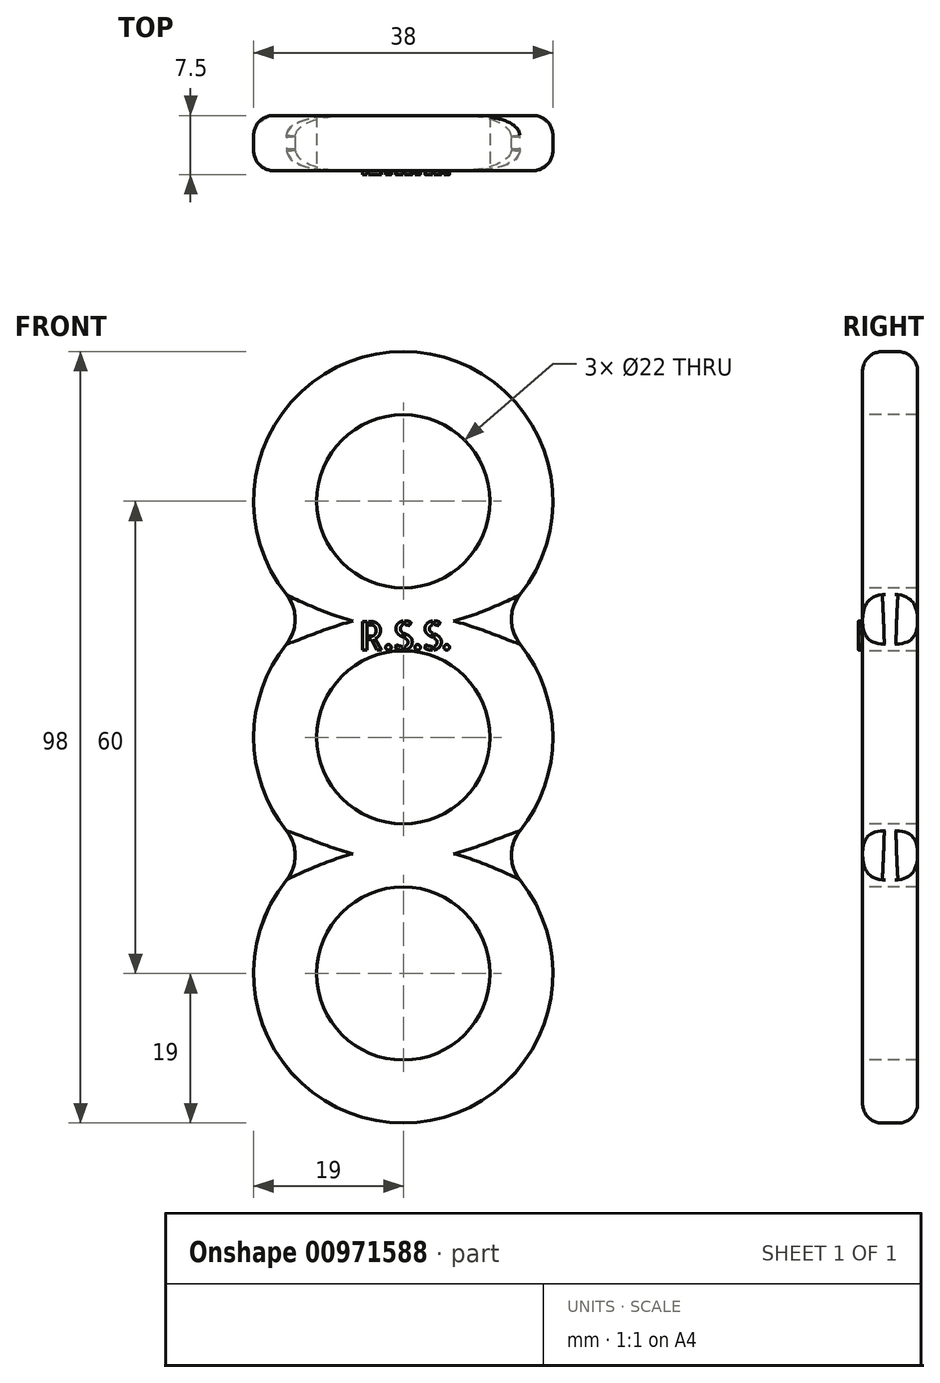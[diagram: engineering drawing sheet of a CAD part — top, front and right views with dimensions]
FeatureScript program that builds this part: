
annotation { "Feature Type Name" : "Feature", "Feature Type Description" : "" }
export const myFeature = defineFeature(function(context is Context, id is Id, definition is map)
    precondition{}
    {
        {
            var Q0;
            Q0=qCreatedBy(makeId("Front.planeOp"),FACE);
            var sketch = newSketch(context, id + "F0", { "sketchPlane" : qUnion([Q0])});
            skCircle(sketch, "E0", {"center": v(0, 0) * mm, "radius": 19 * mm});
            skSolve(sketch);
        }
        {
            var Q0;
            Q0=makeQuery(id+"F0.imprint","IMPRINT",FACE,{"disambiguationData":[TD([[makeQuery(id+"F0.imprint","IMPRINT",EDGE,{"derivedFrom":sQuery(id+"F0.wireOp",EDGE,"E0")}),1.0]])]});
            extrude(context, id + "F1", {"entities" : qUnion([Q0]), "depth" : 7 * mm, "offsetDistance" : 25 * mm});
        }
        {
            var Q0;
            Q0=makeQuery(id+"F1.opExtrude","CAP_FACE",FACE,{"disambiguationData":[OSD([sQuery(id+"F0.wireOp",EDGE,"E0")])],"isStart":false});
            var sketch = newSketch(context, id + "F2", { "sketchPlane" : qUnion([Q0])});
            skCircle(sketch, "E1", {"center": v(0, 0) * mm, "radius": 11 * mm});
            skSolve(sketch);
        }
        {
            var Q0;
            Q0=sQuery(id+"F2.wireOp",VERTEX,"E1.center");
            var Q1;
            Q1=makeQuery(id+"F1.opExtrude","SWEPT_BODY",BODY,{"disambiguationData":[OSD([sQuery(id+"F0.wireOp",EDGE,"E0")])]});
            hole(context, id + "F3", {"style" : HoleStyle.SIMPLE, "endStyle" : HoleEndStyle.THROUGH, "holeDiameter" : 22 * mm, "majorDiameter" : 5 * mm, "isTappedThrough" : true, "tappedDepth" : 12 * mm, "tapClearance" : 3, "locations" : qUnion([Q0]), "scope" : qUnion([Q1])});
        }
        {
            var Q0;
            Q0=qCreatedBy(makeId("Front.planeOp"),FACE);
            var sketch = newSketch(context, id + "F4", { "sketchPlane" : qUnion([Q0])});
            skCircle(sketch, "E2", {"center": v(0, 30) * mm, "radius": 19 * mm});
            skSolve(sketch);
        }
        {
            var Q0;
            Q0=qCreatedBy(makeId("Front.planeOp"),FACE);
            var sketch = newSketch(context, id + "F5", { "sketchPlane" : qUnion([Q0])});
            skCircle(sketch, "E3", {"center": v(0, -30) * mm, "radius": 19 * mm});
            skSolve(sketch);
        }
        {
            var Q0;
            Q0=makeQuery(id+"F4.imprint","IMPRINT",FACE,{"disambiguationData":[TD([[makeQuery(id+"F4.imprint","IMPRINT",EDGE,{"derivedFrom":sQuery(id+"F4.wireOp",EDGE,"E2")}),1.0]])]});
            extrude(context, id + "F6", {"entities" : qUnion([Q0]), "operationType" : NewBodyOperationType.ADD, "depth" : 7 * mm, "offsetDistance" : 25 * mm});
        }
        {
            var Q0;
            Q0=makeQuery(id+"F5.imprint","IMPRINT",FACE,{"disambiguationData":[TD([[makeQuery(id+"F5.imprint","IMPRINT",EDGE,{"derivedFrom":sQuery(id+"F5.wireOp",EDGE,"E3")}),1.0]])]});
            extrude(context, id + "F7", {"entities" : qUnion([Q0]), "operationType" : NewBodyOperationType.ADD, "depth" : 7 * mm, "offsetDistance" : 25 * mm});
        }
        {
            var Q0;
            Q0=makeQuery(id+"F7.boolean.opBoolean","MERGE",FACE,{"derivedFrom":[makeQuery(id+"F6.boolean.opBoolean","MERGE",FACE,{"derivedFrom":[makeQuery(id+"F1.opExtrude","CAP_FACE",FACE,{"disambiguationData":[OSD([sQuery(id+"F0.wireOp",EDGE,"E0")])],"isStart":false}),makeQuery(id+"F6.opExtrude","CAP_FACE",FACE,{"disambiguationData":[OSD([sQuery(id+"F4.wireOp",EDGE,"E2")])],"isStart":false})]}),makeQuery(id+"F7.opExtrude","CAP_FACE",FACE,{"disambiguationData":[OSD([sQuery(id+"F5.wireOp",EDGE,"E3")])],"isStart":false})]});
            var sketch = newSketch(context, id + "F8", { "sketchPlane" : qUnion([Q0])});
            skCircle(sketch, "E4", {"center": v(0, 30) * mm, "radius": 11.47 * mm});
            skSolve(sketch);
        }
        {
            var Q0;
            Q0=sQuery(id+"F8.wireOp",VERTEX,"E4.center");
            var Q1;
            Q1=makeQuery(id+"F1.opExtrude","SWEPT_BODY",BODY,{"disambiguationData":[OSD([sQuery(id+"F0.wireOp",EDGE,"E0")])]});
            hole(context, id + "F9", {"style" : HoleStyle.SIMPLE, "endStyle" : HoleEndStyle.THROUGH, "holeDiameter" : 22 * mm, "majorDiameter" : 5 * mm, "isTappedThrough" : true, "tappedDepth" : 12 * mm, "tapClearance" : 3, "locations" : qUnion([Q0]), "scope" : qUnion([Q1])});
        }
        {
            var Q0;
            Q0=makeQuery(id+"F7.boolean.opBoolean","MERGE",FACE,{"derivedFrom":[makeQuery(id+"F6.boolean.opBoolean","MERGE",FACE,{"derivedFrom":[makeQuery(id+"F1.opExtrude","CAP_FACE",FACE,{"disambiguationData":[OSD([sQuery(id+"F0.wireOp",EDGE,"E0")])],"isStart":false}),makeQuery(id+"F6.opExtrude","CAP_FACE",FACE,{"disambiguationData":[OSD([sQuery(id+"F4.wireOp",EDGE,"E2")])],"isStart":false})]}),makeQuery(id+"F7.opExtrude","CAP_FACE",FACE,{"disambiguationData":[OSD([sQuery(id+"F5.wireOp",EDGE,"E3")])],"isStart":false})]});
            var sketch = newSketch(context, id + "F10", { "sketchPlane" : qUnion([Q0])});
            skCircle(sketch, "E5", {"center": v(0, -30) * mm, "radius": 11.34 * mm});
            skSolve(sketch);
        }
        {
            var Q0;
            Q0=sQuery(id+"F10.wireOp",VERTEX,"E5.center");
            var Q1;
            Q1=makeQuery(id+"F1.opExtrude","SWEPT_BODY",BODY,{"disambiguationData":[OSD([sQuery(id+"F0.wireOp",EDGE,"E0")])]});
            hole(context, id + "F11", {"style" : HoleStyle.SIMPLE, "endStyle" : HoleEndStyle.THROUGH, "holeDiameter" : 22 * mm, "majorDiameter" : 5 * mm, "isTappedThrough" : true, "tappedDepth" : 12 * mm, "tapClearance" : 3, "locations" : qUnion([Q0]), "scope" : qUnion([Q1])});
        }
        {
            var Q0;
            Q0=makeQuery(id+"F6.opExtrude","CAP_EDGE",EDGE,{"disambiguationData":[OSD([sQuery(id+"F4.wireOp",EDGE,"E2")])],"isStart":false});
            fillet(context, id + "F12", {"entities" : qUnion([Q0]), "radius" : 2.5 * mm, "tangentPropagation" : true, "allowEdgeOverflow" : false});
        }
        {
            var Q0;
            Q0=makeQuery(id+"F6.opExtrude","CAP_EDGE",EDGE,{"disambiguationData":[OSD([sQuery(id+"F4.wireOp",EDGE,"E2")])],"isStart":true});
            fillet(context, id + "F13", {"entities" : qUnion([Q0]), "radius" : 2.5 * mm, "tangentPropagation" : true, "allowEdgeOverflow" : false});
        }
        {
            var Q0;
            Q0=makeQuery(id+"F7.boolean.opBoolean","SPLIT",EDGE,{"disambiguationData":[OD(1.0)],"derivedFrom":makeQuery(id+"F1.opExtrude","CAP_EDGE",EDGE,{"disambiguationData":[OSD([sQuery(id+"F0.wireOp",EDGE,"E0")])],"isStart":false})});
            fillet(context, id + "F14", {"entities" : qUnion([Q0]), "radius" : 2.9 * mm, "tangentPropagation" : true, "allowEdgeOverflow" : false});
        }
        {
            var Q0;
            Q0=makeQuery(id+"F7.boolean.opBoolean","SPLIT",EDGE,{"disambiguationData":[OD(0.0)],"derivedFrom":makeQuery(id+"F1.opExtrude","CAP_EDGE",EDGE,{"disambiguationData":[OSD([sQuery(id+"F0.wireOp",EDGE,"E0")])],"isStart":false})});
            fillet(context, id + "F15", {"entities" : qUnion([Q0]), "radius" : 2.9 * mm, "tangentPropagation" : true, "allowEdgeOverflow" : false});
        }
        {
            var Q0;
            Q0=makeQuery(id+"F7.opExtrude","CAP_EDGE",EDGE,{"disambiguationData":[OSD([sQuery(id+"F5.wireOp",EDGE,"E3")])],"isStart":false});
            fillet(context, id + "F16", {"entities" : qUnion([Q0]), "radius" : 2.5 * mm, "tangentPropagation" : true, "allowEdgeOverflow" : false});
        }
        {
            var Q0;
            Q0=makeQuery(id+"F7.boolean.opBoolean","SPLIT",EDGE,{"disambiguationData":[OD(0.0)],"derivedFrom":makeQuery(id+"F1.opExtrude","CAP_EDGE",EDGE,{"disambiguationData":[OSD([sQuery(id+"F0.wireOp",EDGE,"E0")])],"isStart":true})});
            fillet(context, id + "F17", {"entities" : qUnion([Q0]), "radius" : 2.9 * mm, "tangentPropagation" : true, "allowEdgeOverflow" : false});
        }
        {
            var Q0;
            Q0=makeQuery(id+"F7.boolean.opBoolean","SPLIT",EDGE,{"disambiguationData":[OD(1.0)],"derivedFrom":makeQuery(id+"F1.opExtrude","CAP_EDGE",EDGE,{"disambiguationData":[OSD([sQuery(id+"F0.wireOp",EDGE,"E0")])],"isStart":true})});
            fillet(context, id + "F18", {"entities" : qUnion([Q0]), "radius" : 2.9 * mm, "tangentPropagation" : true, "allowEdgeOverflow" : false});
        }
        {
            var Q0;
            Q0=makeQuery(id+"F7.opExtrude","CAP_EDGE",EDGE,{"disambiguationData":[OSD([sQuery(id+"F5.wireOp",EDGE,"E3")])],"isStart":true});
            fillet(context, id + "F19", {"entities" : qUnion([Q0]), "radius" : 2.5 * mm, "tangentPropagation" : true, "allowEdgeOverflow" : false});
        }
        {
            var Q0;
            Q0=qCreatedBy(makeId("Front.planeOp"),FACE);
            var sketch = newSketch(context, id + "F20", { "sketchPlane" : qUnion([Q0])});
            skText(sketch, "E6", { "text": "R.S.S.", "fontName": "AllertaStencil-Regular.ttf"});
            const initialGuessF20  = {"E6": [-0.00565, 0.0111, 1, 0, 0.00364]};
            skSetInitialGuess(sketch, initialGuessF20);
            skSolve(sketch);
        }
        {
            var Q0;
            Q0 = qSketchRegion(id + "F20", true);
            extrude(context, id + "F21", {"entities" : qUnion([Q0]), "operationType" : NewBodyOperationType.ADD, "depth" : 7.5 * mm, "offsetDistance" : 25 * mm});
        }
        {
            var Q0;
            Q0=makeQuery(id+"F14.opFillet","BLEND_FACE",FACE,{"disambiguationData":[OSD([sQuery(id+"F0.wireOp",EDGE,"E0")])]});
            var Q1;
            Q1=makeQuery(id+"F12.opFillet","BLEND_FACE",FACE,{"disambiguationData":[OSD([sQuery(id+"F4.wireOp",EDGE,"E2")])]});
            var Q2;
            Q2=makeQuery(id+"F15.opFillet","BLEND_FACE",FACE,{"disambiguationData":[OSD([sQuery(id+"F0.wireOp",EDGE,"E0")])]});
            fillet(context, id + "F22", {"entities" : qUnion([Q0, Q1, Q2]), "radius" : 5 * mm, "tangentPropagation" : true, "allowEdgeOverflow" : false});
        }
    });
